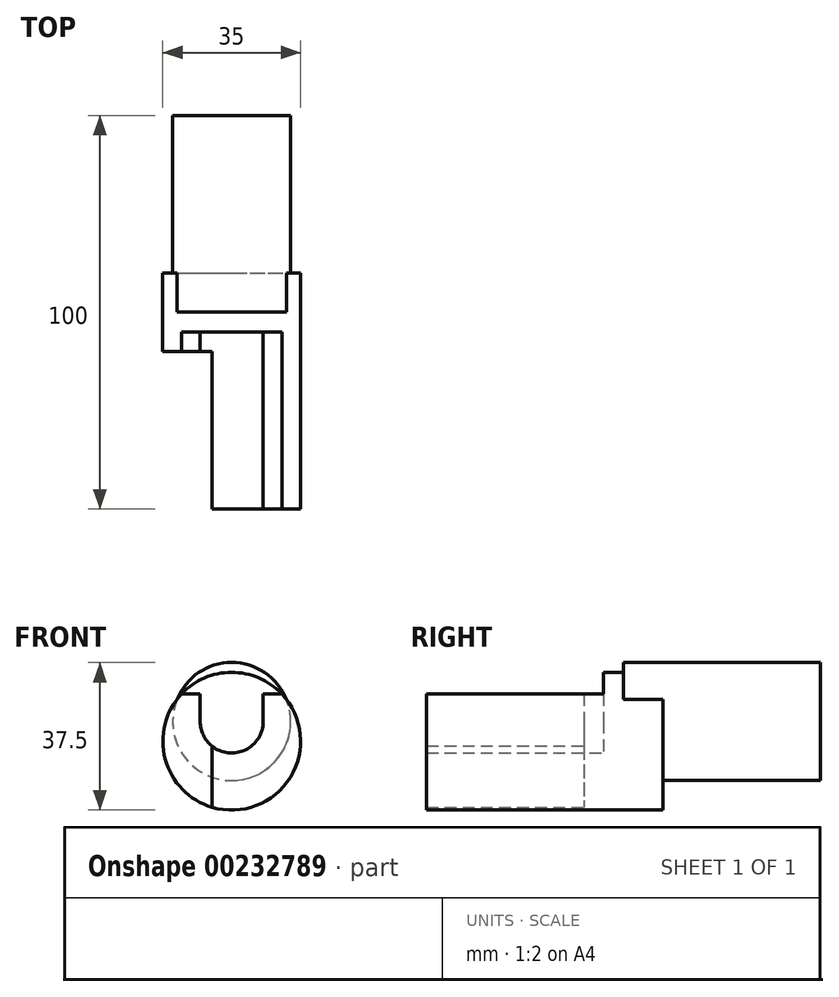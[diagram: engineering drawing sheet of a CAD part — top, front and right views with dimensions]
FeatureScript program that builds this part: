
annotation { "Feature Type Name" : "Feature", "Feature Type Description" : "" }
export const myFeature = defineFeature(function(context is Context, id is Id, definition is map)
    precondition{}
    {
        {
            var Q0;
            Q0=qCreatedBy(makeId("Front.planeOp"),FACE);
            var sketch = newSketch(context, id + "F0", { "sketchPlane" : qUnion([Q0])});
            skCircle(sketch, "E0", {"center": v(0, 0) * mm, "radius": 15 * mm});
            skCircle(sketch, "E1", {"center": v(0, -5) * mm, "radius": 17.5 * mm});
            skLineSegment(sketch, "E2", {"start": v(-12.74, 7) * mm, "end": v(-8, 7) * mm});
            skLineSegment(sketch, "E3", {"start": v(12.74, 7) * mm, "end": v(8, 7) * mm});
            skLineSegment(sketch, "E4", {"start": v(-8, 7) * mm, "end": v(-8, 0) * mm});
            skLineSegment(sketch, "E5", {"start": v(8, 7) * mm, "end": v(8, 0) * mm});
            skArc(sketch, "E6", {"start": v(-8, 0) * mm, "mid": v(0, -8) * mm, "end": v(8, 0) * mm});
            skLineSegment(sketch, "E7", {"start": v(-5, -6.24) * mm, "end": v(-5, -21.77) * mm});
            skSolve(sketch);
        }
        {
            var Q0;
            {var subQ0=sQuery(id+"F0.wireOp",EDGE,"E1");var subQ1=sQuery(id+"F0.wireOp",EDGE,"E0");var subQ2=makeQuery(id+"F0.imprint","INTERSECT",VERTEX,{"disambiguationData":[OD(1.0)],"derivedFrom":[subQ1,subQ0]});Q0=makeQuery(id+"F0.imprint","IMPRINT",FACE,{"disambiguationData":[TD([[makeQuery(id+"F0.imprint","IMPRINT",EDGE,{"disambiguationData":[TD([[subQ2,1.0]])],"derivedFrom":subQ1}),-1.0]])]});}
            var Q1;
            {var subQ1=sQuery(id+"F0.wireOp",EDGE,"E3");Q1=makeQuery(id+"F0.imprint","IMPRINT",FACE,{"disambiguationData":[TD([[makeQuery(id+"F0.imprint","IMPRINT",EDGE,{"derivedFrom":subQ1}),1.0]])]});}
            extrude(context, id + "F1", {"entities" : qUnion([Q0, Q1]), "depth" : 50 * mm});
        }
        {
            var Q0;
            {var subQ1=sQuery(id+"F0.wireOp",EDGE,"E2");Q0=makeQuery(id+"F0.imprint","IMPRINT",FACE,{"disambiguationData":[TD([[makeQuery(id+"F0.imprint","IMPRINT",EDGE,{"derivedFrom":subQ1}),-1.0]])]});}
            var Q1;
            {var subQ0=sQuery(id+"F0.wireOp",EDGE,"E1");var subQ1=sQuery(id+"F0.wireOp",EDGE,"E0");var subQ2=makeQuery(id+"F0.imprint","INTERSECT",VERTEX,{"disambiguationData":[OD(0.0)],"derivedFrom":[subQ1,subQ0]});Q1=makeQuery(id+"F0.imprint","IMPRINT",FACE,{"disambiguationData":[TD([[makeQuery(id+"F0.imprint","IMPRINT",EDGE,{"disambiguationData":[TD([[subQ2,-1.0]])],"derivedFrom":subQ1}),-1.0]])]});}
            extrude(context, id + "F2", {"entities" : qUnion([Q0, Q1]), "operationType" : NewBodyOperationType.ADD, "depth" : 10 * mm});
        }
        {
            var Q0;
            {var subQ2=sQuery(id+"F0.wireOp",EDGE,"E2");Q0=makeQuery(id+"F0.imprint","IMPRINT",FACE,{"disambiguationData":[TD([[makeQuery(id+"F0.imprint","IMPRINT",EDGE,{"derivedFrom":subQ2}),1.0]])]});}
            extrude(context, id + "F3", {"entities" : qUnion([Q0]), "operationType" : NewBodyOperationType.ADD, "depth" : 5 * mm});
        }
        {
            var Q0;
            {var subQ0=sQuery(id+"F0.wireOp",EDGE,"E1");var subQ1=sQuery(id+"F0.wireOp",EDGE,"E0");var subQ2=makeQuery(id+"F0.imprint","INTERSECT",VERTEX,{"disambiguationData":[OD(0.0)],"derivedFrom":[subQ1,subQ0]});Q0=makeQuery(id+"F0.imprint","IMPRINT",FACE,{"disambiguationData":[TD([[makeQuery(id+"F0.imprint","IMPRINT",EDGE,{"disambiguationData":[TD([[subQ2,-1.0]])],"derivedFrom":subQ1}),-1.0]])]});}
            extrude(context, id + "F4", {"entities" : qUnion([Q0]), "operationType" : NewBodyOperationType.ADD, "oppositeDirection" : true, "depth" : 10 * mm});
        }
        {
            var Q0;
            {var subQ0=sQuery(id+"F0.wireOp",EDGE,"E1");var subQ1=sQuery(id+"F0.wireOp",EDGE,"E0");var subQ2=makeQuery(id+"F0.imprint","INTERSECT",VERTEX,{"disambiguationData":[OD(0.0)],"derivedFrom":[subQ1,subQ0]});Q0=makeQuery(id+"F0.imprint","IMPRINT",FACE,{"disambiguationData":[TD([[makeQuery(id+"F0.imprint","IMPRINT",EDGE,{"disambiguationData":[TD([[subQ2,1.0]])],"derivedFrom":subQ1}),1.0]])]});}
            var Q1;
            {var subQ2=sQuery(id+"F0.wireOp",EDGE,"E2");Q1=makeQuery(id+"F0.imprint","IMPRINT",FACE,{"disambiguationData":[TD([[makeQuery(id+"F0.imprint","IMPRINT",EDGE,{"derivedFrom":subQ2}),1.0]])]});}
            var Q2;
            {var subQ1=sQuery(id+"F0.wireOp",EDGE,"E3");Q2=makeQuery(id+"F0.imprint","IMPRINT",FACE,{"disambiguationData":[TD([[makeQuery(id+"F0.imprint","IMPRINT",EDGE,{"derivedFrom":subQ1}),1.0]])]});}
            var Q3;
            {var subQ1=sQuery(id+"F0.wireOp",EDGE,"E2");Q3=makeQuery(id+"F0.imprint","IMPRINT",FACE,{"disambiguationData":[TD([[makeQuery(id+"F0.imprint","IMPRINT",EDGE,{"derivedFrom":subQ1}),-1.0]])]});}
            extrude(context, id + "F5", {"entities" : qUnion([Q0, Q1, Q2, Q3]), "operationType" : NewBodyOperationType.ADD, "oppositeDirection" : true, "depth" : 50 * mm});
        }
        {
            var Q0;
            Q0 = qSketchRegion(id + "F0", true);
            var Q1;
            {var subQ0=sQuery(id+"F0.wireOp",EDGE,"E1");var subQ1=sQuery(id+"F0.wireOp",EDGE,"E0");var subQ2=makeQuery(id+"F0.imprint","INTERSECT",VERTEX,{"disambiguationData":[OD(1.0)],"derivedFrom":[subQ1,subQ0]});Q1=makeQuery(id+"F0.imprint","IMPRINT",FACE,{"disambiguationData":[TD([[makeQuery(id+"F0.imprint","IMPRINT",EDGE,{"disambiguationData":[TD([[subQ2,1.0]])],"derivedFrom":subQ1}),-1.0]])]});}
            extrude(context, id + "F6", {"entities" : qUnion([Q0, Q1]), "operationType" : NewBodyOperationType.ADD, "oppositeDirection" : true, "depth" : 10 * mm});
        }
    });
